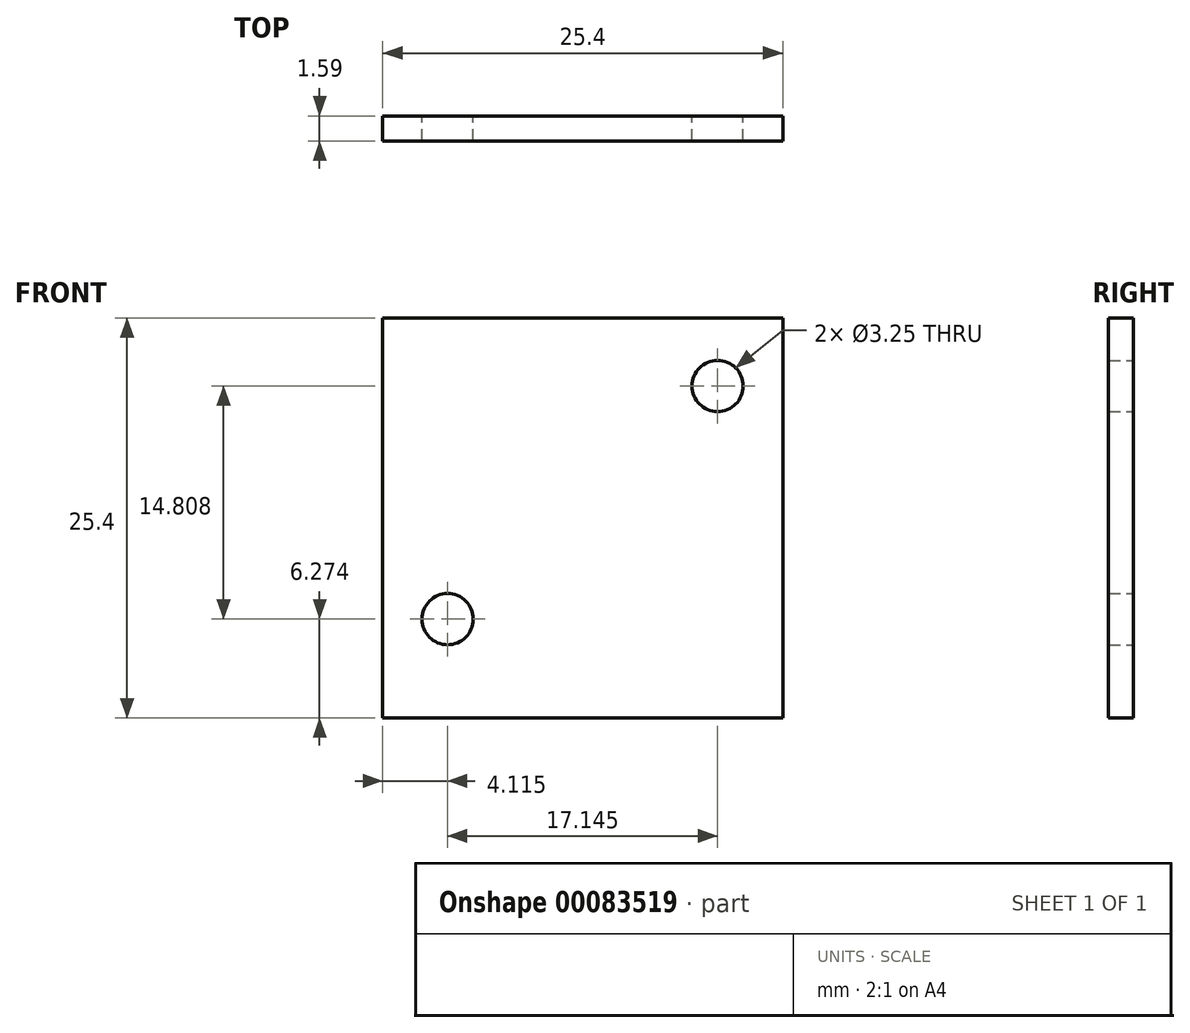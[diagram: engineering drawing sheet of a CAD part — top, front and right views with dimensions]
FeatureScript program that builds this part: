
annotation { "Feature Type Name" : "Feature", "Feature Type Description" : "" }
export const myFeature = defineFeature(function(context is Context, id is Id, definition is map)
    precondition{}
    {
        {
            var Q0;
            Q0=qCreatedBy(makeId("Front.planeOp"),FACE);
            var sketch = newSketch(context, id + "F0", { "sketchPlane" : qUnion([Q0])});
            skLineSegment(sketch, "E0.bottom", {"start": v(-12.7, 12.7) * mm, "end": v(12.7, 12.7) * mm});
            skLineSegment(sketch, "E0.top", {"start": v(-12.7, -12.7) * mm, "end": v(12.7, -12.7) * mm});
            skLineSegment(sketch, "E0.left", {"start": v(-12.7, 12.7) * mm, "end": v(-12.7, -12.7) * mm});
            skLineSegment(sketch, "E0.right", {"start": v(12.7, 12.7) * mm, "end": v(12.7, -12.7) * mm});
            skPoint(sketch, "E0.middle", {"position": v(0, 0) * mm});
            skLineSegment(sketch, "E1", {"start": v(-8.59, -6.43) * mm, "end": v(13.37, -6.43) * mm});
            skLineSegment(sketch, "E2", {"start": v(8.56, -17.9) * mm, "end": v(8.56, 8.38) * mm});
            skLineSegment(sketch, "E3", {"start": v(0, -15.19) * mm, "end": v(0, 17.18) * mm});
            skPoint(sketch, "E3.endSnap0", {"position": v(0, 12.7) * mm});
            skSolve(sketch);
        }
        {
            var Q0;
            {var subQ4=sQuery(id+"F0.wireOp",EDGE,"E0.left");Q0=makeQuery(id+"F0.imprint","IMPRINT",FACE,{"disambiguationData":[TD([[makeQuery(id+"F0.imprint","IMPRINT",EDGE,{"derivedFrom":subQ4}),1.0]])]});}
            var Q1;
            {var subQ1=sQuery(id+"F0.wireOp",EDGE,"E0.right");var subQ6=sQuery(id+"F0.wireOp",EDGE,"E0.bottom");var subQ7=makeQuery(id+"F0.imprint","INTERSECT",VERTEX,{"derivedFrom":[subQ6,subQ1]});Q1=makeQuery(id+"F0.imprint","IMPRINT",FACE,{"disambiguationData":[TD([[makeQuery(id+"F0.imprint","IMPRINT",EDGE,{"disambiguationData":[TD([[subQ7,1.0]])],"derivedFrom":subQ6}),-1.0]])]});}
            var Q2;
            {var subQ0=sQuery(id+"F0.wireOp",EDGE,"E3");var subQ1=sQuery(id+"F0.wireOp",EDGE,"E0.top");var subQ2=makeQuery(id+"F0.imprint","INTERSECT",VERTEX,{"derivedFrom":[subQ1,subQ0]});Q2=makeQuery(id+"F0.imprint","IMPRINT",FACE,{"disambiguationData":[TD([[makeQuery(id+"F0.imprint","IMPRINT",EDGE,{"disambiguationData":[TD([[subQ2,-1.0]])],"derivedFrom":subQ1}),1.0]])]});}
            var Q3;
            {var subQ0=sQuery(id+"F0.wireOp",EDGE,"E0.right");var subQ1=sQuery(id+"F0.wireOp",EDGE,"E0.top");var subQ2=makeQuery(id+"F0.imprint","INTERSECT",VERTEX,{"derivedFrom":[subQ1,subQ0]});Q3=makeQuery(id+"F0.imprint","IMPRINT",FACE,{"disambiguationData":[TD([[makeQuery(id+"F0.imprint","IMPRINT",EDGE,{"disambiguationData":[TD([[subQ2,1.0]])],"derivedFrom":subQ1}),1.0]])]});}
            extrude(context, id + "F1", {"entities" : qUnion([Q0, Q1, Q2, Q3]), "depth" : 1.59 * mm});
        }
        {
            var Q0;
            Q0=sQuery(id+"F0.wireOp",VERTEX,"E2.end");
            var Q1;
            Q1=sQuery(id+"F0.wireOp",VERTEX,"E1.start");
            var Q2;
            Q2=makeQuery(id+"F1.opExtrude","SWEPT_BODY",BODY,{"disambiguationData":[OSD([sQuery(id+"F0.wireOp",EDGE,"E0.bottom"),sQuery(id+"F0.wireOp",EDGE,"E0.top"),sQuery(id+"F0.wireOp",EDGE,"E0.left"),sQuery(id+"F0.wireOp",EDGE,"E0.right")])]});
            hole(context, id + "F2", {"style" : HoleStyle.SIMPLE, "endStyle" : HoleEndStyle.THROUGH, "oppositeDirection" : true, "holeDiameter" : 3.25 * mm, "locations" : qUnion([Q0, Q1]), "scope" : qUnion([Q2]), "isTappedThrough" : true});
        }
    });
